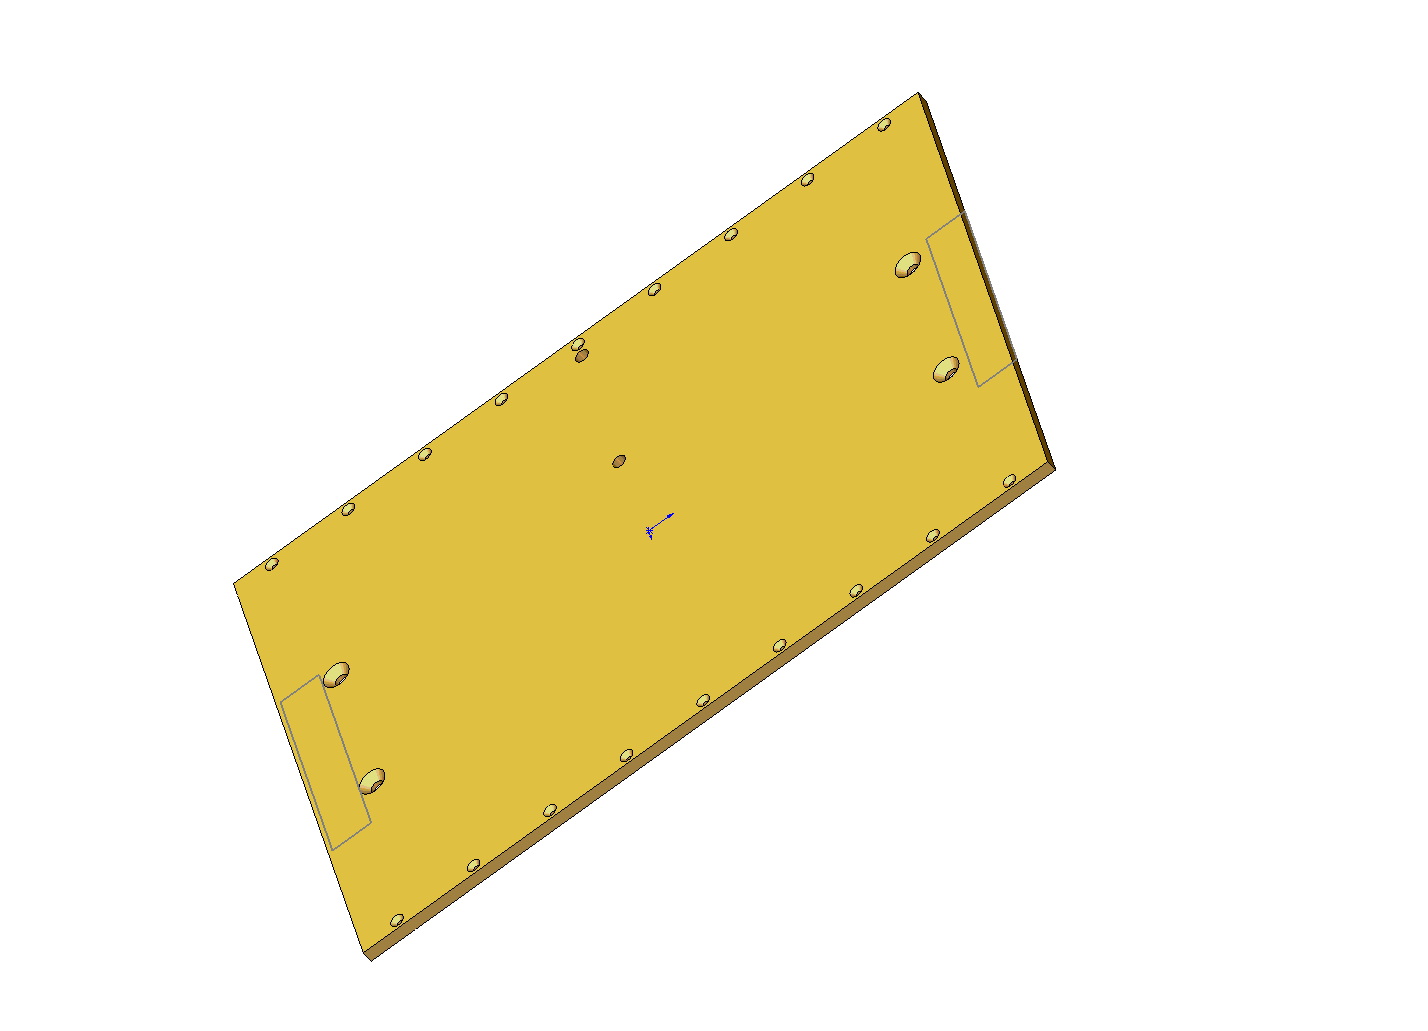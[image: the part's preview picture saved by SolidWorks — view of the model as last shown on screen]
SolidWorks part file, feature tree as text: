
SOLIDWORKS PART (.sldprt)
format: sldprt  version: not decoded by parser v0  size: 487,936 bytes
history: native  units: mm
features: sketch x8, hole x3, material x1, extrude x1 (+12 scaffold rows collapsed)
feature tree (25):
  scaffold x12  (default folders/planes/origin — collapsed)
  material  "Material <not specified>"
  sketch  "Sketch1"  dims[c1.D1=355.6mm c1.D2=1.27mm c1.D3=1.27mm c2.D2=31.75mm c2.D3=31.75mm c3.D2=12.7mm c3.D3=12.7mm c4.D2=25.4mm c4.D3=25.4mm]
  extrude  "Extrude1"  Depth=7.9375mm
  sketch  "Sketch2"  dims[c1.D1=~1.269955mm c1.D2=1.27mm c1.D3=1.27mm c1.D4=1.27mm c1.D5=~1.275109mm c1.D6=1.27mm c2.D2=1.27mm c2.D1=1.27mm c2.D5=2.54mm c2.D6=2.54mm c3.D2=1.27mm c3.D3=2.54mm c3.D4=2.54mm]
  hole  "5/16 Clearance Hole1"  Diameter=8.72998mm Depth=7.9375mm
  sketch  "Sketch11"  dims[D1=101.6mm]
  sketch  "Sketch10"  dims[hole-wizard template sketch: 59 standard entries collapsed; hole parameters kept: c18.Thru Hole Dia.=~8.72998mm c18.Thru Hole Depth=7.9375mm]
  hole  "CSK for 5/16 Flat Head Socket Cap Screw1"  Diameter=8.4328mm Depth=7.9375mm
  sketch  "Sketch13"
  sketch  "Sketch12"  dims[hole-wizard template sketch: 54 standard entries collapsed; hole parameters kept: c17.Thru Hole Dia.=8.4328mm c17.Thru Hole Depth=7.9375mm c17.Near C'Sink Dia.=~17.545583mm c17.D4=~3.666174mm c17.Near C'Sink Angle=82.0deg]
  hole  "CSK for #6 Flat Head Socket Cap Screw1"  Diameter=3.6576mm Depth=7.938008mm
  sketch  "Sketch15"  dims[D1=6.35mm D2=6.35mm D3=53.975mm]
  sketch  "Sketch14"  dims[hole-wizard template sketch: 39 standard entries collapsed; hole parameters kept: c13.Hole Dia.=3.6576mm c13.Hole Depth=~7.938008mm c13.Near C'Sink Dia.=~8.680983mm c13.D4=~33.297463mm c13.Near C'Sink Angle=82.0deg c14.D5=~14.816244mm c14.Drill Angle=118.0deg]
decode coverage: 11 of 12 modeling features carry decoded parameters
note: ~ marks probable driven/reference dimensions
note: suppression state not decoded; provenance and decode notes live in map.json
